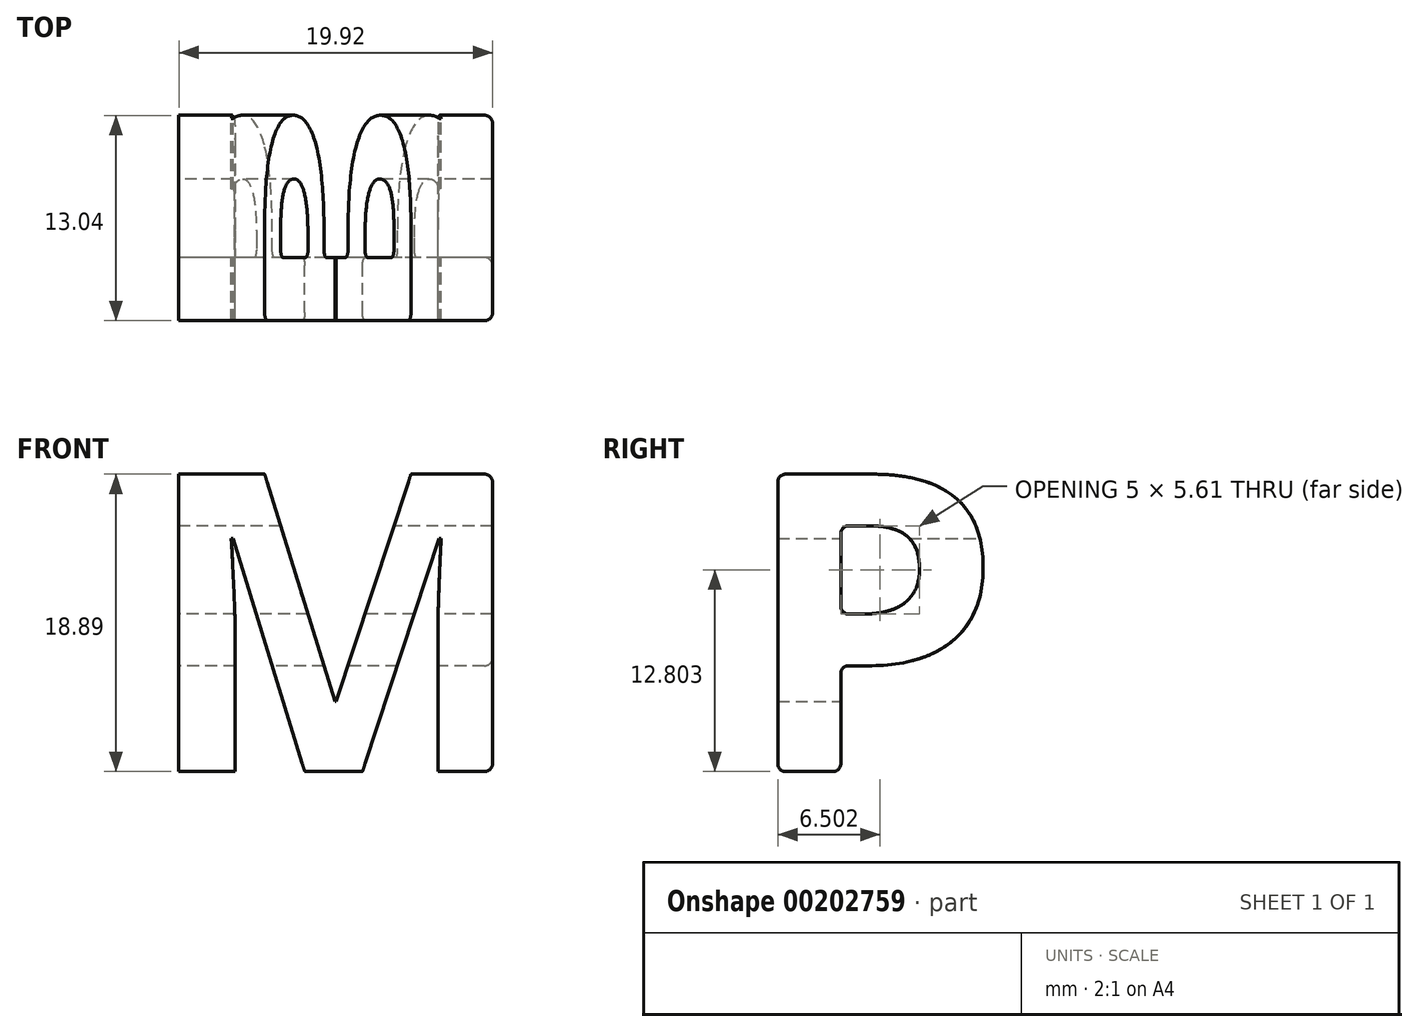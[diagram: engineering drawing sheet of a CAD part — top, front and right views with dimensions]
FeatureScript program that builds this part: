
annotation { "Feature Type Name" : "Feature", "Feature Type Description" : "" }
export const myFeature = defineFeature(function(context is Context, id is Id, definition is map)
    precondition{}
    {
        {
            var Q0;
            Q0=qCreatedBy(makeId("Right.planeOp"),FACE);
            var sketch = newSketch(context, id + "F0", { "sketchPlane" : qUnion([Q0])});
            skText(sketch, "E0", { "text": "P", "fontName": "OpenSans-Bold.ttf"});
            const initialGuessF0  = {"E0": [-0.00857, 0, 1, 0, 0.01905]};
            skSetInitialGuess(sketch, initialGuessF0);
            skSolve(sketch);
        }
        {
            var Q0;
            Q0 = qSketchRegion(id + "F0", true);
            extrude(context, id + "F1", {"entities" : qUnion([Q0]), "depth" : 10.16 * mm, "hasSecondDirection" : true, "secondDirectionOppositeDirection" : true, "secondDirectionDepth" : 10.16 * mm});
        }
        {
            var Q0;
            Q0=qCreatedBy(makeId("Front.planeOp"),FACE);
            var sketch = newSketch(context, id + "F2", { "sketchPlane" : qUnion([Q0])});
            skText(sketch, "E1", { "text": "M", "fontName": "OpenSans-Bold.ttf"});
            const initialGuessF2  = {"E1": [-0.01214, 0, 1, 0, 0.01905]};
            skSetInitialGuess(sketch, initialGuessF2);
            skSolve(sketch);
        }
        {
            var Q0;
            Q0 = qSketchRegion(id + "F2", true);
            extrude(context, id + "F3", {"entities" : qUnion([Q0]), "operationType" : NewBodyOperationType.INTERSECT, "endBound" : BoundingType.THROUGH_ALL, "depth" : 25.4 * mm, "hasSecondDirection" : true, "secondDirectionBound" : SecondDirectionBoundingType.THROUGH_ALL, "secondDirectionOppositeDirection" : true, "secondDirectionDepth" : 25.4 * mm});
        }
        {
            var Q0;
            Q0=makeQuery(id+"F1.opExtrude","SWEPT_EDGE",EDGE,{"disambiguationData":[OSD([sQuery(id+"F0.wireOp",EDGE,"E0.sketch_text.stroke-0"),sQuery(id+"F0.wireOp",EDGE,"E0.sketch_text.stroke-6")])]});
            var Q1;
            Q1=makeQuery(id+"F1.opExtrude","SWEPT_EDGE",EDGE,{"disambiguationData":[OSD([sQuery(id+"F0.wireOp",EDGE,"E0.sketch_text.stroke-5"),sQuery(id+"F0.wireOp",EDGE,"E0.sketch_text.stroke-6")])]});
            var Q2;
            Q2=makeQuery(id+"F1.opExtrude","SWEPT_EDGE",EDGE,{"disambiguationData":[OSD([sQuery(id+"F0.wireOp",EDGE,"E0.sketch_text.stroke-9"),sQuery(id+"F0.wireOp",EDGE,"E0.sketch_text.stroke-10")])]});
            var Q3;
            Q3=makeQuery(id+"F1.opExtrude","SWEPT_EDGE",EDGE,{"disambiguationData":[OSD([sQuery(id+"F0.wireOp",EDGE,"E0.sketch_text.stroke-10"),sQuery(id+"F0.wireOp",EDGE,"E0.sketch_text.stroke-11")])]});
            var Q4;
            Q4=makeQuery(id+"F1.opExtrude","SWEPT_EDGE",EDGE,{"disambiguationData":[OSD([sQuery(id+"F0.wireOp",EDGE,"E0.sketch_text.stroke-11"),sQuery(id+"F0.wireOp",EDGE,"E0.sketch_text.stroke-12")])]});
            var Q5;
            Q5=makeQuery(id+"F1.opExtrude","SWEPT_EDGE",EDGE,{"disambiguationData":[OSD([sQuery(id+"F0.wireOp",EDGE,"E0.sketch_text.stroke-12"),sQuery(id+"F0.wireOp",EDGE,"E0.sketch_text.stroke-13")])]});
            fillet(context, id + "F4", {"entities" : qUnion([Q0, Q1, Q2, Q3, Q4, Q5]), "radius" : 0.5 * mm, "tangentPropagation" : true, "allowEdgeOverflow" : false});
        }
        {
            var Q0;
            Q0=makeQuery(id+"F3.boolean.opBoolean","INTERSECT",EDGE,{"derivedFrom":[makeQuery(id+"F1.opExtrude","SWEPT_FACE",FACE,{"disambiguationData":[OSD([sQuery(id+"F0.wireOp",EDGE,"E0.sketch_text.stroke-15")])]}),makeQuery(id+"F3.boolean.toolComplement.opBoolean","COPY",FACE,{"derivedFrom":makeQuery(id+"F3.opExtrude","SWEPT_FACE",FACE,{"disambiguationData":[OSD([sQuery(id+"F2.wireOp",EDGE,"E1.sketch_text.stroke-7")])]})})]});
            var Q1;
            Q1=makeQuery(id+"F3.boolean.opBoolean","INTERSECT",EDGE,{"derivedFrom":[makeQuery(id+"F1.opExtrude","SWEPT_FACE",FACE,{"disambiguationData":[OSD([sQuery(id+"F0.wireOp",EDGE,"E0.sketch_text.stroke-15")])]}),makeQuery(id+"F3.boolean.toolComplement.opBoolean","COPY",FACE,{"derivedFrom":makeQuery(id+"F3.opExtrude","SWEPT_FACE",FACE,{"disambiguationData":[OSD([sQuery(id+"F2.wireOp",EDGE,"E1.sketch_text.stroke-5")])]})})]});
            var Q2;
            Q2=makeQuery(id+"F3.boolean.opBoolean","INTERSECT",EDGE,{"derivedFrom":[makeQuery(id+"F1.opExtrude","SWEPT_FACE",FACE,{"disambiguationData":[OSD([sQuery(id+"F0.wireOp",EDGE,"E0.sketch_text.stroke-15")])]}),makeQuery(id+"F3.boolean.toolComplement.opBoolean","COPY",FACE,{"derivedFrom":makeQuery(id+"F3.opExtrude","SWEPT_FACE",FACE,{"disambiguationData":[OSD([sQuery(id+"F2.wireOp",EDGE,"E1.sketch_text.stroke-9")])]})})]});
            var Q3;
            Q3=makeQuery(id+"F1.opExtrude","CAP_EDGE",EDGE,{"disambiguationData":[OSD([sQuery(id+"F0.wireOp",EDGE,"E0.sketch_text.stroke-15")])],"isStart":false});
            var Q4;
            Q4=makeQuery(id+"F3.boolean.opBoolean","INTERSECT",EDGE,{"derivedFrom":[makeQuery(id+"F1.opExtrude","SWEPT_FACE",FACE,{"disambiguationData":[OSD([sQuery(id+"F0.wireOp",EDGE,"E0.sketch_text.stroke-12")])]}),makeQuery(id+"F3.boolean.toolComplement.opBoolean","COPY",FACE,{"derivedFrom":makeQuery(id+"F3.opExtrude","SWEPT_FACE",FACE,{"disambiguationData":[OSD([sQuery(id+"F2.wireOp",EDGE,"E1.sketch_text.stroke-3")])]})})]});
            var Q5;
            Q5=makeQuery(id+"F3.boolean.opBoolean","INTERSECT",EDGE,{"derivedFrom":[makeQuery(id+"F1.opExtrude","SWEPT_FACE",FACE,{"disambiguationData":[OSD([sQuery(id+"F0.wireOp",EDGE,"E0.sketch_text.stroke-12")])]}),makeQuery(id+"F3.boolean.toolComplement.opBoolean","COPY",FACE,{"derivedFrom":makeQuery(id+"F3.opExtrude","SWEPT_FACE",FACE,{"disambiguationData":[OSD([sQuery(id+"F2.wireOp",EDGE,"E1.sketch_text.stroke-0")])]})})]});
            var Q6;
            Q6=makeQuery(id+"F3.boolean.opBoolean","INTERSECT",EDGE,{"derivedFrom":[makeQuery(id+"F1.opExtrude","SWEPT_FACE",FACE,{"disambiguationData":[OSD([sQuery(id+"F0.wireOp",EDGE,"E0.sketch_text.stroke-12")])]}),makeQuery(id+"F3.boolean.toolComplement.opBoolean","COPY",FACE,{"derivedFrom":makeQuery(id+"F3.opExtrude","SWEPT_FACE",FACE,{"disambiguationData":[OSD([sQuery(id+"F2.wireOp",EDGE,"E1.sketch_text.stroke-17")])]})})]});
            var Q7;
            Q7=makeQuery(id+"F3.boolean.opBoolean","INTERSECT",EDGE,{"derivedFrom":[makeQuery(id+"F1.opExtrude","SWEPT_FACE",FACE,{"disambiguationData":[OSD([sQuery(id+"F0.wireOp",EDGE,"E0.sketch_text.stroke-12")])]}),makeQuery(id+"F3.boolean.toolComplement.opBoolean","COPY",FACE,{"derivedFrom":makeQuery(id+"F3.opExtrude","SWEPT_FACE",FACE,{"disambiguationData":[OSD([sQuery(id+"F2.wireOp",EDGE,"E1.sketch_text.stroke-13")])]})})]});
            fillet(context, id + "F5", {"entities" : qUnion([Q0, Q1, Q2, Q3, Q4, Q5, Q6, Q7]), "radius" : 0.5 * mm, "tangentPropagation" : true, "allowEdgeOverflow" : false});
        }
    });
